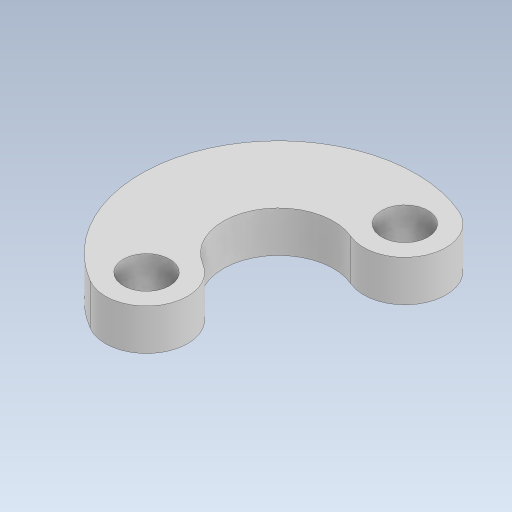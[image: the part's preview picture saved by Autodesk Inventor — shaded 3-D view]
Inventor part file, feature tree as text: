
AUTODESK INVENTOR PART (.ipt)
format: ipt  version: 2023 (Build 270158000, 158)  size: 121,344 bytes
history: native  units: in
note: dims shown in document units (in); Inventor stores cm internally (conversion verified against a paired STEP export)
features: sketch x2, extrude x1, hole x1
ambient origin geometry x8: Origin, YZ Plane, XZ Plane, XY Plane, X Axis, Y Axis, Z Axis, Center Point
bodies: Solid1 (feature_tree)
feature tree (4):
  extrude  "Extrusion1"  Depth=0.5in
  hole  "Hole1"  [1 undecoded]
  sketch  "Sketch1"  dims[d0=0.4724in d1=0.5in]
  sketch  "Sketch2"  dims[d2=0.9843in d3=135.0deg d4=0.2362in d5=0.0in d6=0.2362in d7=0.266in d8=0.2362in d9=0.507in d10=0.0787in d11=0.5635in d12=0.5in d13=0.8108in d17=0.3169in]
note: 1 required parameter value undecoded (feature->parameter linkage not recoverable at this tier; creation-order binding heuristic only, values carry confidence <= 0.55)
